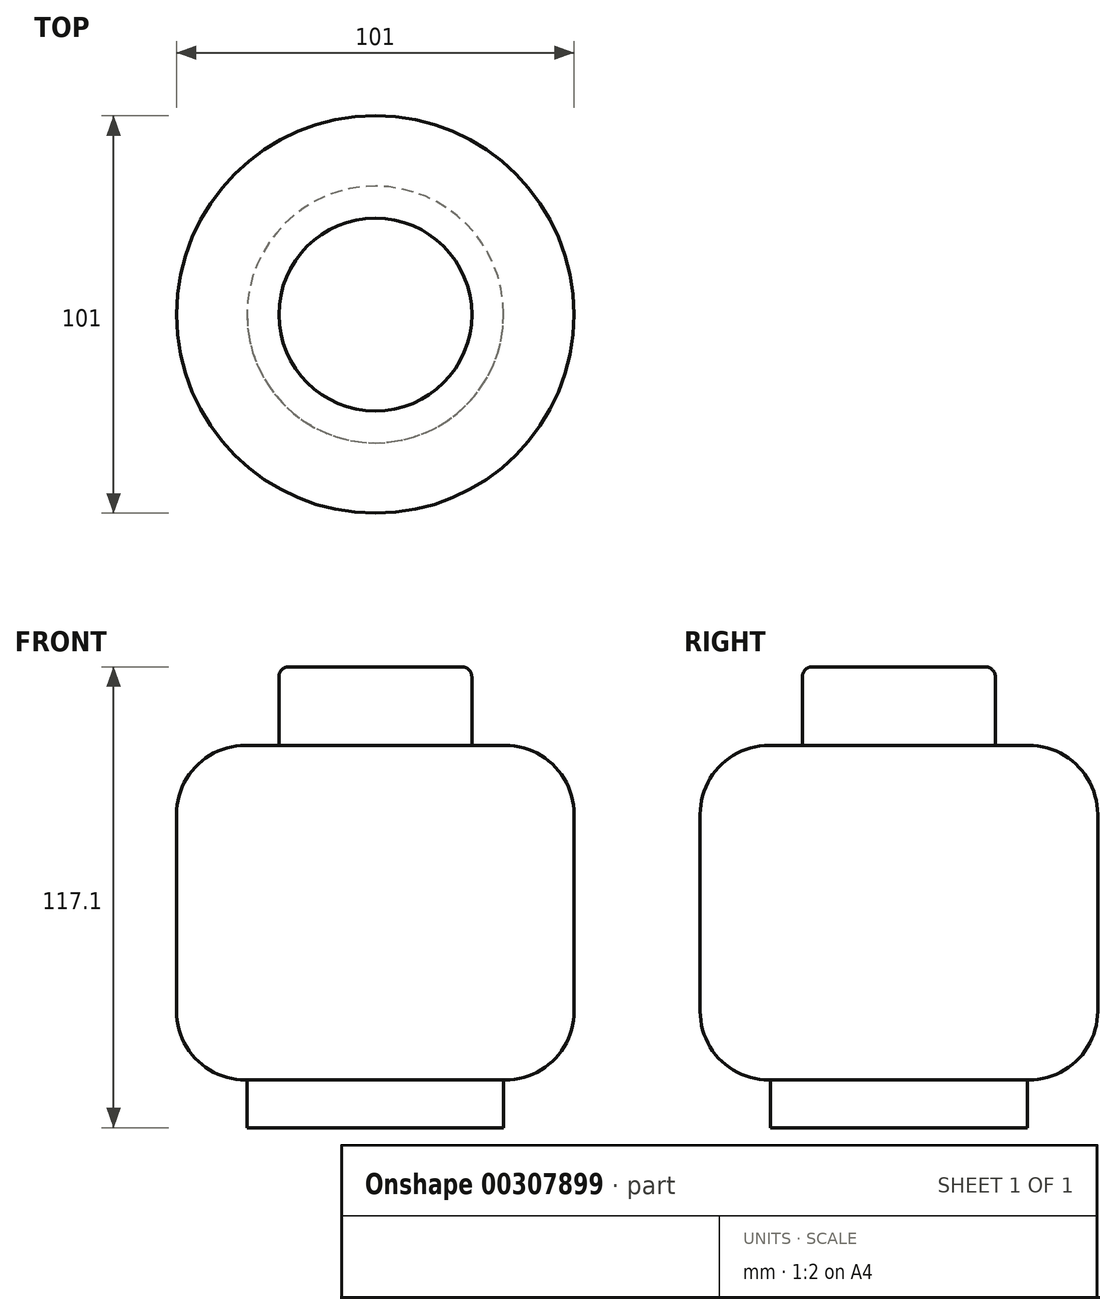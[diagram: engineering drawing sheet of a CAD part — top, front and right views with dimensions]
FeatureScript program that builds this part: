
annotation { "Feature Type Name" : "Feature", "Feature Type Description" : "" }
export const myFeature = defineFeature(function(context is Context, id is Id, definition is map)
    precondition{}
    {
        {
            var Q0;
            Q0=qCreatedBy(makeId("Top.planeOp"),FACE);
            var sketch = newSketch(context, id + "F0", { "sketchPlane" : qUnion([Q0])});
            skCircle(sketch, "E0", {"center": v(0, 0) * mm, "radius": 50.5 * mm});
            skSolve(sketch);
        }
        {
            var Q0;
            Q0 = qSketchRegion(id + "F0", true);
            extrude(context, id + "F1", {"entities" : qUnion([Q0]), "depth" : 85 * mm});
        }
        {
            var Q0;
            Q0=makeQuery(id+"F1.opExtrude","SWEPT_FACE",FACE,{"disambiguationData":[OSD([sQuery(id+"F0.wireOp",EDGE,"E0")])]});
            fillet(context, id + "F2", {"entities" : qUnion([Q0]), "radius" : 17.5 * mm, "tangentPropagation" : true, "allowEdgeOverflow" : false});
        }
        {
            var Q0;
            Q0=makeQuery(id+"F1.opExtrude","CAP_FACE",FACE,{"disambiguationData":[OSD([sQuery(id+"F0.wireOp",EDGE,"E0")])],"isStart":false});
            var sketch = newSketch(context, id + "F3", { "sketchPlane" : qUnion([Q0])});
            skCircle(sketch, "E1", {"center": v(0, 0) * mm, "radius": 24.5 * mm});
            skSolve(sketch);
        }
        {
            var Q0;
            Q0 = qSketchRegion(id + "F3", true);
            extrude(context, id + "F4", {"entities" : qUnion([Q0]), "operationType" : NewBodyOperationType.ADD, "depth" : 20 * mm});
        }
        {
            var Q0;
            Q0=makeQuery(id+"F4.opExtrude","CAP_EDGE",EDGE,{"disambiguationData":[OSD([sQuery(id+"F3.wireOp",EDGE,"E1")])],"isStart":false});
            fillet(context, id + "F5", {"entities" : qUnion([Q0]), "radius" : 2.5 * mm, "tangentPropagation" : true, "allowEdgeOverflow" : false});
        }
        {
            var Q0;
            Q0=makeQuery(id+"F1.opExtrude","CAP_FACE",FACE,{"disambiguationData":[OSD([sQuery(id+"F0.wireOp",EDGE,"E0")])],"isStart":true});
            var sketch = newSketch(context, id + "F6", { "sketchPlane" : qUnion([Q0])});
            skCircle(sketch, "E2", {"center": v(0, 0) * mm, "radius": 32.6 * mm});
            skSolve(sketch);
        }
        {
            var Q0;
            Q0 = qSketchRegion(id + "F6", true);
            extrude(context, id + "F7", {"entities" : qUnion([Q0]), "operationType" : NewBodyOperationType.ADD, "depth" : 12.1 * mm});
        }
    });
